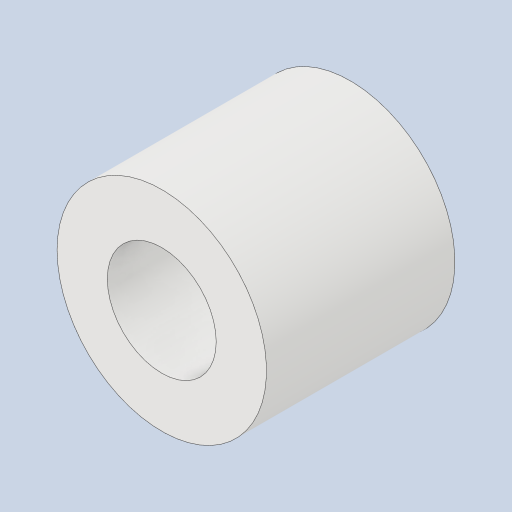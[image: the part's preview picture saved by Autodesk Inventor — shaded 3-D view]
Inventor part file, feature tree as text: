
AUTODESK INVENTOR PART (.ipt)
format: ipt  version: 2023 (Build 270158000, 158)  size: 129,024 bytes
history: native  units: mm
features: sketch x2, revolve x1, hole x1
ambient origin geometry x8: Origin, YZ Plane, XZ Plane, XY Plane, X Axis, Y Axis, Z Axis, Center Point
bodies: Solid1 (feature_tree)
feature tree (4):
  revolve  "Revolution1"  [1 undecoded]
  hole  "Hole1"  [1 undecoded]
  sketch  "Sketch_1"  dims[d0=360.0deg]
  sketch  "Sketch2"  dims[d1=2.6mm d2=6.0mm d3=4.0mm d4=2.0mm d5=90.0deg d6=4.5mm d7=0.0mm]
note: 2 required parameter values undecoded (feature->parameter linkage not recoverable at this tier; creation-order binding heuristic only, values carry confidence <= 0.55)
